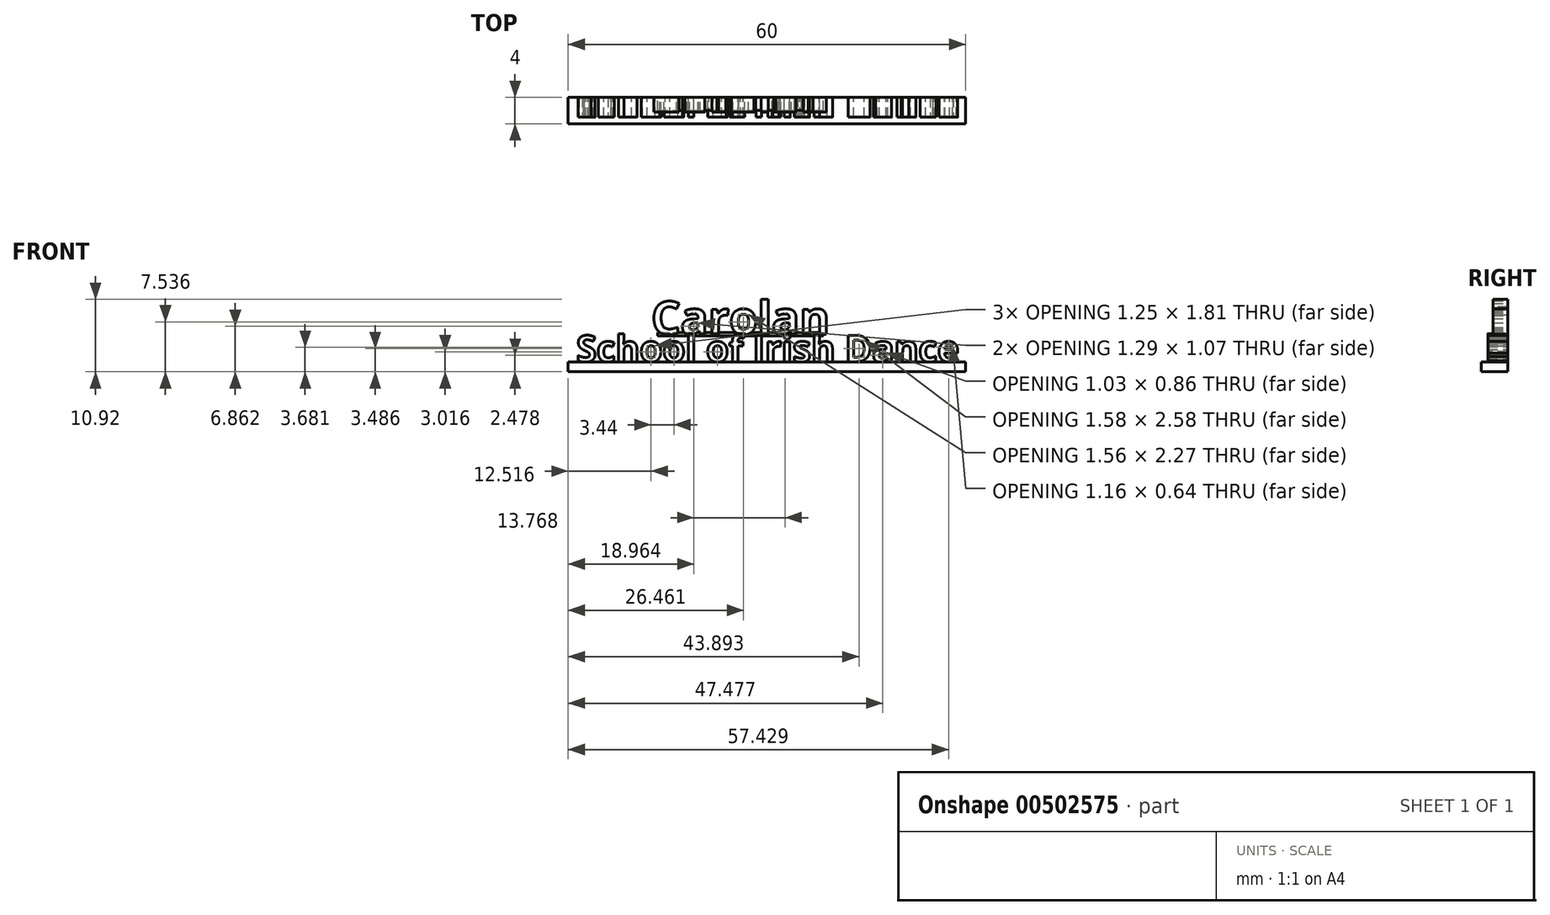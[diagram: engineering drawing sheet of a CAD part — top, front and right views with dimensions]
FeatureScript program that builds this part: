
annotation { "Feature Type Name" : "Feature", "Feature Type Description" : "" }
export const myFeature = defineFeature(function(context is Context, id is Id, definition is map)
    precondition{}
    {
        {
            var Q0;
            Q0=qCreatedBy(makeId("Front.planeOp"),FACE);
            var sketch = newSketch(context, id + "F0", { "sketchPlane" : qUnion([Q0])});
            skLineSegment(sketch, "E0.bottom", {"start": v(-37.8, -3.94) * mm, "end": v(22.2, -3.94) * mm});
            skLineSegment(sketch, "E0.top", {"start": v(-37.8, -5.44) * mm, "end": v(22.2, -5.44) * mm});
            skLineSegment(sketch, "E0.left", {"start": v(-37.8, -3.94) * mm, "end": v(-37.8, -5.44) * mm});
            skLineSegment(sketch, "E0.right", {"start": v(22.2, -3.94) * mm, "end": v(22.2, -5.44) * mm});
            skSolve(sketch);
        }
        {
            var Q0;
            Q0=makeQuery(id+"F0.imprint","IMPRINT",FACE,{"disambiguationData":[TD([[makeQuery(id+"F0.imprint","IMPRINT",EDGE,{"derivedFrom":sQuery(id+"F0.wireOp",EDGE,"E0.bottom")}),-1.0]])]});
            extrude(context, id + "F1", {"entities" : qUnion([Q0]), "depth" : 4 * mm, "offsetDistance" : 25 * mm});
        }
        {
            var Q0;
            Q0=qCreatedBy(makeId("Front.planeOp"),FACE);
            var sketch = newSketch(context, id + "F2", { "sketchPlane" : qUnion([Q0])});
            skText(sketch, "E1", { "text": "School of Irish Dance", "fontName": "OpenSans-Bold.ttf"});
            const initialGuessF2  = {"E1": [-0.02696, 0.00286, 1, 0, 0.004]};
            skSetInitialGuess(sketch, initialGuessF2);
            skSolve(sketch);
        }
        {
            var Q0;
            Q0 = qSketchRegion(id + "F2", true);
            extrude(context, id + "F3", {"entities" : qUnion([Q0]), "depth" : 3 * mm, "offsetDistance" : 25 * mm});
        }
        {
            var Q0;
            Q0=makeQuery(id+"F3.opExtrude","SWEPT_BODY",BODY,{"disambiguationData":[OSD([sQuery(id+"F2.wireOp",EDGE,"E1.sketch_text.stroke-0"),sQuery(id+"F2.wireOp",EDGE,"E1.sketch_text.stroke-1"),sQuery(id+"F2.wireOp",EDGE,"E1.sketch_text.stroke-2"),sQuery(id+"F2.wireOp",EDGE,"E1.sketch_text.stroke-3"),sQuery(id+"F2.wireOp",EDGE,"E1.sketch_text.stroke-4"),sQuery(id+"F2.wireOp",EDGE,"E1.sketch_text.stroke-5"),sQuery(id+"F2.wireOp",EDGE,"E1.sketch_text.stroke-6"),sQuery(id+"F2.wireOp",EDGE,"E1.sketch_text.stroke-7"),sQuery(id+"F2.wireOp",EDGE,"E1.sketch_text.stroke-8"),sQuery(id+"F2.wireOp",EDGE,"E1.sketch_text.stroke-9"),sQuery(id+"F2.wireOp",EDGE,"E1.sketch_text.stroke-10"),sQuery(id+"F2.wireOp",EDGE,"E1.sketch_text.stroke-11"),sQuery(id+"F2.wireOp",EDGE,"E1.sketch_text.stroke-12"),sQuery(id+"F2.wireOp",EDGE,"E1.sketch_text.stroke-13"),sQuery(id+"F2.wireOp",EDGE,"E1.sketch_text.stroke-14"),sQuery(id+"F2.wireOp",EDGE,"E1.sketch_text.stroke-15"),sQuery(id+"F2.wireOp",EDGE,"E1.sketch_text.stroke-16"),sQuery(id+"F2.wireOp",EDGE,"E1.sketch_text.stroke-17"),sQuery(id+"F2.wireOp",EDGE,"E1.sketch_text.stroke-18"),sQuery(id+"F2.wireOp",EDGE,"E1.sketch_text.stroke-19"),sQuery(id+"F2.wireOp",EDGE,"E1.sketch_text.stroke-20"),sQuery(id+"F2.wireOp",EDGE,"E1.sketch_text.stroke-21"),sQuery(id+"F2.wireOp",EDGE,"E1.sketch_text.stroke-22"),sQuery(id+"F2.wireOp",EDGE,"E1.sketch_text.stroke-23"),sQuery(id+"F2.wireOp",EDGE,"E1.sketch_text.stroke-24"),sQuery(id+"F2.wireOp",EDGE,"E1.sketch_text.stroke-25"),sQuery(id+"F2.wireOp",EDGE,"E1.sketch_text.stroke-26"),sQuery(id+"F2.wireOp",EDGE,"E1.sketch_text.stroke-27")])]});
            var Q1;
            Q1=makeQuery(id+"F3.opExtrude","SWEPT_BODY",BODY,{"disambiguationData":[OSD([sQuery(id+"F2.wireOp",EDGE,"E1.sketch_text.stroke-28"),sQuery(id+"F2.wireOp",EDGE,"E1.sketch_text.stroke-29"),sQuery(id+"F2.wireOp",EDGE,"E1.sketch_text.stroke-30"),sQuery(id+"F2.wireOp",EDGE,"E1.sketch_text.stroke-31"),sQuery(id+"F2.wireOp",EDGE,"E1.sketch_text.stroke-32"),sQuery(id+"F2.wireOp",EDGE,"E1.sketch_text.stroke-33"),sQuery(id+"F2.wireOp",EDGE,"E1.sketch_text.stroke-34"),sQuery(id+"F2.wireOp",EDGE,"E1.sketch_text.stroke-35"),sQuery(id+"F2.wireOp",EDGE,"E1.sketch_text.stroke-36"),sQuery(id+"F2.wireOp",EDGE,"E1.sketch_text.stroke-37"),sQuery(id+"F2.wireOp",EDGE,"E1.sketch_text.stroke-38"),sQuery(id+"F2.wireOp",EDGE,"E1.sketch_text.stroke-39"),sQuery(id+"F2.wireOp",EDGE,"E1.sketch_text.stroke-40"),sQuery(id+"F2.wireOp",EDGE,"E1.sketch_text.stroke-41")])]});
            var Q2;
            Q2=makeQuery(id+"F3.opExtrude","SWEPT_BODY",BODY,{"disambiguationData":[OSD([sQuery(id+"F2.wireOp",EDGE,"E1.sketch_text.stroke-42"),sQuery(id+"F2.wireOp",EDGE,"E1.sketch_text.stroke-43"),sQuery(id+"F2.wireOp",EDGE,"E1.sketch_text.stroke-44"),sQuery(id+"F2.wireOp",EDGE,"E1.sketch_text.stroke-45"),sQuery(id+"F2.wireOp",EDGE,"E1.sketch_text.stroke-46"),sQuery(id+"F2.wireOp",EDGE,"E1.sketch_text.stroke-47"),sQuery(id+"F2.wireOp",EDGE,"E1.sketch_text.stroke-48"),sQuery(id+"F2.wireOp",EDGE,"E1.sketch_text.stroke-49"),sQuery(id+"F2.wireOp",EDGE,"E1.sketch_text.stroke-50"),sQuery(id+"F2.wireOp",EDGE,"E1.sketch_text.stroke-51"),sQuery(id+"F2.wireOp",EDGE,"E1.sketch_text.stroke-52"),sQuery(id+"F2.wireOp",EDGE,"E1.sketch_text.stroke-53"),sQuery(id+"F2.wireOp",EDGE,"E1.sketch_text.stroke-54"),sQuery(id+"F2.wireOp",EDGE,"E1.sketch_text.stroke-55"),sQuery(id+"F2.wireOp",EDGE,"E1.sketch_text.stroke-56"),sQuery(id+"F2.wireOp",EDGE,"E1.sketch_text.stroke-57"),sQuery(id+"F2.wireOp",EDGE,"E1.sketch_text.stroke-58")])]});
            var Q3;
            Q3=makeQuery(id+"F3.opExtrude","SWEPT_BODY",BODY,{"disambiguationData":[OSD([sQuery(id+"F2.wireOp",EDGE,"E1.sketch_text.stroke-59"),sQuery(id+"F2.wireOp",EDGE,"E1.sketch_text.stroke-60"),sQuery(id+"F2.wireOp",EDGE,"E1.sketch_text.stroke-61"),sQuery(id+"F2.wireOp",EDGE,"E1.sketch_text.stroke-62"),sQuery(id+"F2.wireOp",EDGE,"E1.sketch_text.stroke-63"),sQuery(id+"F2.wireOp",EDGE,"E1.sketch_text.stroke-64"),sQuery(id+"F2.wireOp",EDGE,"E1.sketch_text.stroke-65"),sQuery(id+"F2.wireOp",EDGE,"E1.sketch_text.stroke-66"),sQuery(id+"F2.wireOp",EDGE,"E1.sketch_text.stroke-67"),sQuery(id+"F2.wireOp",EDGE,"E1.sketch_text.stroke-68"),sQuery(id+"F2.wireOp",EDGE,"E1.sketch_text.stroke-69"),sQuery(id+"F2.wireOp",EDGE,"E1.sketch_text.stroke-70"),sQuery(id+"F2.wireOp",EDGE,"E1.sketch_text.stroke-71"),sQuery(id+"F2.wireOp",EDGE,"E1.sketch_text.stroke-72"),sQuery(id+"F2.wireOp",EDGE,"E1.sketch_text.stroke-73"),sQuery(id+"F2.wireOp",EDGE,"E1.sketch_text.stroke-74"),sQuery(id+"F2.wireOp",EDGE,"E1.sketch_text.stroke-75"),sQuery(id+"F2.wireOp",EDGE,"E1.sketch_text.stroke-76")])]});
            var Q4;
            Q4=makeQuery(id+"F3.opExtrude","SWEPT_BODY",BODY,{"disambiguationData":[OSD([sQuery(id+"F2.wireOp",EDGE,"E1.sketch_text.stroke-77"),sQuery(id+"F2.wireOp",EDGE,"E1.sketch_text.stroke-78"),sQuery(id+"F2.wireOp",EDGE,"E1.sketch_text.stroke-79"),sQuery(id+"F2.wireOp",EDGE,"E1.sketch_text.stroke-80"),sQuery(id+"F2.wireOp",EDGE,"E1.sketch_text.stroke-81"),sQuery(id+"F2.wireOp",EDGE,"E1.sketch_text.stroke-82"),sQuery(id+"F2.wireOp",EDGE,"E1.sketch_text.stroke-83"),sQuery(id+"F2.wireOp",EDGE,"E1.sketch_text.stroke-84"),sQuery(id+"F2.wireOp",EDGE,"E1.sketch_text.stroke-85"),sQuery(id+"F2.wireOp",EDGE,"E1.sketch_text.stroke-86"),sQuery(id+"F2.wireOp",EDGE,"E1.sketch_text.stroke-87"),sQuery(id+"F2.wireOp",EDGE,"E1.sketch_text.stroke-88"),sQuery(id+"F2.wireOp",EDGE,"E1.sketch_text.stroke-89"),sQuery(id+"F2.wireOp",EDGE,"E1.sketch_text.stroke-90"),sQuery(id+"F2.wireOp",EDGE,"E1.sketch_text.stroke-91"),sQuery(id+"F2.wireOp",EDGE,"E1.sketch_text.stroke-92"),sQuery(id+"F2.wireOp",EDGE,"E1.sketch_text.stroke-93"),sQuery(id+"F2.wireOp",EDGE,"E1.sketch_text.stroke-94")])]});
            var Q5;
            Q5=makeQuery(id+"F3.opExtrude","SWEPT_BODY",BODY,{"disambiguationData":[OSD([sQuery(id+"F2.wireOp",EDGE,"E1.sketch_text.stroke-95"),sQuery(id+"F2.wireOp",EDGE,"E1.sketch_text.stroke-96"),sQuery(id+"F2.wireOp",EDGE,"E1.sketch_text.stroke-97"),sQuery(id+"F2.wireOp",EDGE,"E1.sketch_text.stroke-98")])]});
            var Q6;
            Q6=makeQuery(id+"F3.opExtrude","SWEPT_BODY",BODY,{"disambiguationData":[OSD([sQuery(id+"F2.wireOp",EDGE,"E1.sketch_text.stroke-99"),sQuery(id+"F2.wireOp",EDGE,"E1.sketch_text.stroke-100"),sQuery(id+"F2.wireOp",EDGE,"E1.sketch_text.stroke-101"),sQuery(id+"F2.wireOp",EDGE,"E1.sketch_text.stroke-102"),sQuery(id+"F2.wireOp",EDGE,"E1.sketch_text.stroke-103"),sQuery(id+"F2.wireOp",EDGE,"E1.sketch_text.stroke-104"),sQuery(id+"F2.wireOp",EDGE,"E1.sketch_text.stroke-105"),sQuery(id+"F2.wireOp",EDGE,"E1.sketch_text.stroke-106"),sQuery(id+"F2.wireOp",EDGE,"E1.sketch_text.stroke-107"),sQuery(id+"F2.wireOp",EDGE,"E1.sketch_text.stroke-108"),sQuery(id+"F2.wireOp",EDGE,"E1.sketch_text.stroke-109"),sQuery(id+"F2.wireOp",EDGE,"E1.sketch_text.stroke-110"),sQuery(id+"F2.wireOp",EDGE,"E1.sketch_text.stroke-111"),sQuery(id+"F2.wireOp",EDGE,"E1.sketch_text.stroke-112"),sQuery(id+"F2.wireOp",EDGE,"E1.sketch_text.stroke-113"),sQuery(id+"F2.wireOp",EDGE,"E1.sketch_text.stroke-114"),sQuery(id+"F2.wireOp",EDGE,"E1.sketch_text.stroke-115"),sQuery(id+"F2.wireOp",EDGE,"E1.sketch_text.stroke-116")])]});
            var Q7;
            Q7=makeQuery(id+"F3.opExtrude","SWEPT_BODY",BODY,{"disambiguationData":[OSD([sQuery(id+"F2.wireOp",EDGE,"E1.sketch_text.stroke-117"),sQuery(id+"F2.wireOp",EDGE,"E1.sketch_text.stroke-118"),sQuery(id+"F2.wireOp",EDGE,"E1.sketch_text.stroke-119"),sQuery(id+"F2.wireOp",EDGE,"E1.sketch_text.stroke-120"),sQuery(id+"F2.wireOp",EDGE,"E1.sketch_text.stroke-121"),sQuery(id+"F2.wireOp",EDGE,"E1.sketch_text.stroke-122"),sQuery(id+"F2.wireOp",EDGE,"E1.sketch_text.stroke-123"),sQuery(id+"F2.wireOp",EDGE,"E1.sketch_text.stroke-124"),sQuery(id+"F2.wireOp",EDGE,"E1.sketch_text.stroke-125"),sQuery(id+"F2.wireOp",EDGE,"E1.sketch_text.stroke-126"),sQuery(id+"F2.wireOp",EDGE,"E1.sketch_text.stroke-127"),sQuery(id+"F2.wireOp",EDGE,"E1.sketch_text.stroke-128"),sQuery(id+"F2.wireOp",EDGE,"E1.sketch_text.stroke-129"),sQuery(id+"F2.wireOp",EDGE,"E1.sketch_text.stroke-130"),sQuery(id+"F2.wireOp",EDGE,"E1.sketch_text.stroke-131"),sQuery(id+"F2.wireOp",EDGE,"E1.sketch_text.stroke-132"),sQuery(id+"F2.wireOp",EDGE,"E1.sketch_text.stroke-133"),sQuery(id+"F2.wireOp",EDGE,"E1.sketch_text.stroke-134")])]});
            var Q8;
            Q8=makeQuery(id+"F3.opExtrude","SWEPT_BODY",BODY,{"disambiguationData":[OSD([sQuery(id+"F2.wireOp",EDGE,"E1.sketch_text.stroke-135"),sQuery(id+"F2.wireOp",EDGE,"E1.sketch_text.stroke-136"),sQuery(id+"F2.wireOp",EDGE,"E1.sketch_text.stroke-137"),sQuery(id+"F2.wireOp",EDGE,"E1.sketch_text.stroke-138")])]});
            var Q9;
            Q9=makeQuery(id+"F3.opExtrude","SWEPT_BODY",BODY,{"disambiguationData":[OSD([sQuery(id+"F2.wireOp",EDGE,"E1.sketch_text.stroke-139"),sQuery(id+"F2.wireOp",EDGE,"E1.sketch_text.stroke-140"),sQuery(id+"F2.wireOp",EDGE,"E1.sketch_text.stroke-141"),sQuery(id+"F2.wireOp",EDGE,"E1.sketch_text.stroke-142"),sQuery(id+"F2.wireOp",EDGE,"E1.sketch_text.stroke-143"),sQuery(id+"F2.wireOp",EDGE,"E1.sketch_text.stroke-144"),sQuery(id+"F2.wireOp",EDGE,"E1.sketch_text.stroke-145"),sQuery(id+"F2.wireOp",EDGE,"E1.sketch_text.stroke-146"),sQuery(id+"F2.wireOp",EDGE,"E1.sketch_text.stroke-147"),sQuery(id+"F2.wireOp",EDGE,"E1.sketch_text.stroke-148"),sQuery(id+"F2.wireOp",EDGE,"E1.sketch_text.stroke-149"),sQuery(id+"F2.wireOp",EDGE,"E1.sketch_text.stroke-150"),sQuery(id+"F2.wireOp",EDGE,"E1.sketch_text.stroke-151")])]});
            var Q10;
            Q10=makeQuery(id+"F3.opExtrude","SWEPT_BODY",BODY,{"disambiguationData":[OSD([sQuery(id+"F2.wireOp",EDGE,"E1.sketch_text.stroke-152"),sQuery(id+"F2.wireOp",EDGE,"E1.sketch_text.stroke-153"),sQuery(id+"F2.wireOp",EDGE,"E1.sketch_text.stroke-154"),sQuery(id+"F2.wireOp",EDGE,"E1.sketch_text.stroke-155"),sQuery(id+"F2.wireOp",EDGE,"E1.sketch_text.stroke-156")])]});
            var Q11;
            Q11=makeQuery(id+"F3.opExtrude","SWEPT_BODY",BODY,{"disambiguationData":[OSD([sQuery(id+"F2.wireOp",EDGE,"E1.sketch_text.stroke-157"),sQuery(id+"F2.wireOp",EDGE,"E1.sketch_text.stroke-158"),sQuery(id+"F2.wireOp",EDGE,"E1.sketch_text.stroke-159"),sQuery(id+"F2.wireOp",EDGE,"E1.sketch_text.stroke-160")])]});
            var Q12;
            Q12=makeQuery(id+"F3.opExtrude","SWEPT_BODY",BODY,{"disambiguationData":[OSD([sQuery(id+"F2.wireOp",EDGE,"E1.sketch_text.stroke-161"),sQuery(id+"F2.wireOp",EDGE,"E1.sketch_text.stroke-162"),sQuery(id+"F2.wireOp",EDGE,"E1.sketch_text.stroke-163"),sQuery(id+"F2.wireOp",EDGE,"E1.sketch_text.stroke-164"),sQuery(id+"F2.wireOp",EDGE,"E1.sketch_text.stroke-165"),sQuery(id+"F2.wireOp",EDGE,"E1.sketch_text.stroke-166"),sQuery(id+"F2.wireOp",EDGE,"E1.sketch_text.stroke-167"),sQuery(id+"F2.wireOp",EDGE,"E1.sketch_text.stroke-168"),sQuery(id+"F2.wireOp",EDGE,"E1.sketch_text.stroke-169"),sQuery(id+"F2.wireOp",EDGE,"E1.sketch_text.stroke-170"),sQuery(id+"F2.wireOp",EDGE,"E1.sketch_text.stroke-171"),sQuery(id+"F2.wireOp",EDGE,"E1.sketch_text.stroke-172"),sQuery(id+"F2.wireOp",EDGE,"E1.sketch_text.stroke-173"),sQuery(id+"F2.wireOp",EDGE,"E1.sketch_text.stroke-174"),sQuery(id+"F2.wireOp",EDGE,"E1.sketch_text.stroke-175"),sQuery(id+"F2.wireOp",EDGE,"E1.sketch_text.stroke-176"),sQuery(id+"F2.wireOp",EDGE,"E1.sketch_text.stroke-177"),sQuery(id+"F2.wireOp",EDGE,"E1.sketch_text.stroke-178"),sQuery(id+"F2.wireOp",EDGE,"E1.sketch_text.stroke-179"),sQuery(id+"F2.wireOp",EDGE,"E1.sketch_text.stroke-180"),sQuery(id+"F2.wireOp",EDGE,"E1.sketch_text.stroke-181"),sQuery(id+"F2.wireOp",EDGE,"E1.sketch_text.stroke-182"),sQuery(id+"F2.wireOp",EDGE,"E1.sketch_text.stroke-183"),sQuery(id+"F2.wireOp",EDGE,"E1.sketch_text.stroke-184"),sQuery(id+"F2.wireOp",EDGE,"E1.sketch_text.stroke-185"),sQuery(id+"F2.wireOp",EDGE,"E1.sketch_text.stroke-186")])]});
            var Q13;
            Q13=makeQuery(id+"F3.opExtrude","SWEPT_BODY",BODY,{"disambiguationData":[OSD([sQuery(id+"F2.wireOp",EDGE,"E1.sketch_text.stroke-187"),sQuery(id+"F2.wireOp",EDGE,"E1.sketch_text.stroke-188"),sQuery(id+"F2.wireOp",EDGE,"E1.sketch_text.stroke-189"),sQuery(id+"F2.wireOp",EDGE,"E1.sketch_text.stroke-190"),sQuery(id+"F2.wireOp",EDGE,"E1.sketch_text.stroke-191"),sQuery(id+"F2.wireOp",EDGE,"E1.sketch_text.stroke-192"),sQuery(id+"F2.wireOp",EDGE,"E1.sketch_text.stroke-193"),sQuery(id+"F2.wireOp",EDGE,"E1.sketch_text.stroke-194"),sQuery(id+"F2.wireOp",EDGE,"E1.sketch_text.stroke-195"),sQuery(id+"F2.wireOp",EDGE,"E1.sketch_text.stroke-196"),sQuery(id+"F2.wireOp",EDGE,"E1.sketch_text.stroke-197"),sQuery(id+"F2.wireOp",EDGE,"E1.sketch_text.stroke-198"),sQuery(id+"F2.wireOp",EDGE,"E1.sketch_text.stroke-199"),sQuery(id+"F2.wireOp",EDGE,"E1.sketch_text.stroke-200"),sQuery(id+"F2.wireOp",EDGE,"E1.sketch_text.stroke-201"),sQuery(id+"F2.wireOp",EDGE,"E1.sketch_text.stroke-202"),sQuery(id+"F2.wireOp",EDGE,"E1.sketch_text.stroke-203")])]});
            var Q14;
            Q14=makeQuery(id+"F3.opExtrude","SWEPT_BODY",BODY,{"disambiguationData":[OSD([sQuery(id+"F2.wireOp",EDGE,"E1.sketch_text.stroke-204"),sQuery(id+"F2.wireOp",EDGE,"E1.sketch_text.stroke-205"),sQuery(id+"F2.wireOp",EDGE,"E1.sketch_text.stroke-206"),sQuery(id+"F2.wireOp",EDGE,"E1.sketch_text.stroke-207"),sQuery(id+"F2.wireOp",EDGE,"E1.sketch_text.stroke-208"),sQuery(id+"F2.wireOp",EDGE,"E1.sketch_text.stroke-209"),sQuery(id+"F2.wireOp",EDGE,"E1.sketch_text.stroke-210"),sQuery(id+"F2.wireOp",EDGE,"E1.sketch_text.stroke-211"),sQuery(id+"F2.wireOp",EDGE,"E1.sketch_text.stroke-212"),sQuery(id+"F2.wireOp",EDGE,"E1.sketch_text.stroke-213"),sQuery(id+"F2.wireOp",EDGE,"E1.sketch_text.stroke-214"),sQuery(id+"F2.wireOp",EDGE,"E1.sketch_text.stroke-215")])]});
            var Q15;
            Q15=makeQuery(id+"F3.opExtrude","SWEPT_BODY",BODY,{"disambiguationData":[OSD([sQuery(id+"F2.wireOp",EDGE,"E1.sketch_text.stroke-216"),sQuery(id+"F2.wireOp",EDGE,"E1.sketch_text.stroke-217"),sQuery(id+"F2.wireOp",EDGE,"E1.sketch_text.stroke-218"),sQuery(id+"F2.wireOp",EDGE,"E1.sketch_text.stroke-219"),sQuery(id+"F2.wireOp",EDGE,"E1.sketch_text.stroke-220"),sQuery(id+"F2.wireOp",EDGE,"E1.sketch_text.stroke-221"),sQuery(id+"F2.wireOp",EDGE,"E1.sketch_text.stroke-222"),sQuery(id+"F2.wireOp",EDGE,"E1.sketch_text.stroke-223"),sQuery(id+"F2.wireOp",EDGE,"E1.sketch_text.stroke-224"),sQuery(id+"F2.wireOp",EDGE,"E1.sketch_text.stroke-225"),sQuery(id+"F2.wireOp",EDGE,"E1.sketch_text.stroke-226"),sQuery(id+"F2.wireOp",EDGE,"E1.sketch_text.stroke-227"),sQuery(id+"F2.wireOp",EDGE,"E1.sketch_text.stroke-228"),sQuery(id+"F2.wireOp",EDGE,"E1.sketch_text.stroke-229"),sQuery(id+"F2.wireOp",EDGE,"E1.sketch_text.stroke-230"),sQuery(id+"F2.wireOp",EDGE,"E1.sketch_text.stroke-231"),sQuery(id+"F2.wireOp",EDGE,"E1.sketch_text.stroke-232"),sQuery(id+"F2.wireOp",EDGE,"E1.sketch_text.stroke-233"),sQuery(id+"F2.wireOp",EDGE,"E1.sketch_text.stroke-234"),sQuery(id+"F2.wireOp",EDGE,"E1.sketch_text.stroke-235"),sQuery(id+"F2.wireOp",EDGE,"E1.sketch_text.stroke-236"),sQuery(id+"F2.wireOp",EDGE,"E1.sketch_text.stroke-237"),sQuery(id+"F2.wireOp",EDGE,"E1.sketch_text.stroke-238"),sQuery(id+"F2.wireOp",EDGE,"E1.sketch_text.stroke-239"),sQuery(id+"F2.wireOp",EDGE,"E1.sketch_text.stroke-240")])]});
            var Q16;
            Q16=makeQuery(id+"F3.opExtrude","SWEPT_BODY",BODY,{"disambiguationData":[OSD([sQuery(id+"F2.wireOp",EDGE,"E1.sketch_text.stroke-241"),sQuery(id+"F2.wireOp",EDGE,"E1.sketch_text.stroke-242"),sQuery(id+"F2.wireOp",EDGE,"E1.sketch_text.stroke-243"),sQuery(id+"F2.wireOp",EDGE,"E1.sketch_text.stroke-244"),sQuery(id+"F2.wireOp",EDGE,"E1.sketch_text.stroke-245"),sQuery(id+"F2.wireOp",EDGE,"E1.sketch_text.stroke-246"),sQuery(id+"F2.wireOp",EDGE,"E1.sketch_text.stroke-247"),sQuery(id+"F2.wireOp",EDGE,"E1.sketch_text.stroke-248"),sQuery(id+"F2.wireOp",EDGE,"E1.sketch_text.stroke-249"),sQuery(id+"F2.wireOp",EDGE,"E1.sketch_text.stroke-250"),sQuery(id+"F2.wireOp",EDGE,"E1.sketch_text.stroke-251"),sQuery(id+"F2.wireOp",EDGE,"E1.sketch_text.stroke-252"),sQuery(id+"F2.wireOp",EDGE,"E1.sketch_text.stroke-253"),sQuery(id+"F2.wireOp",EDGE,"E1.sketch_text.stroke-254"),sQuery(id+"F2.wireOp",EDGE,"E1.sketch_text.stroke-255"),sQuery(id+"F2.wireOp",EDGE,"E1.sketch_text.stroke-256"),sQuery(id+"F2.wireOp",EDGE,"E1.sketch_text.stroke-257")])]});
            var Q17;
            Q17=makeQuery(id+"F3.opExtrude","SWEPT_BODY",BODY,{"disambiguationData":[OSD([sQuery(id+"F2.wireOp",EDGE,"E1.sketch_text.stroke-258"),sQuery(id+"F2.wireOp",EDGE,"E1.sketch_text.stroke-259"),sQuery(id+"F2.wireOp",EDGE,"E1.sketch_text.stroke-260"),sQuery(id+"F2.wireOp",EDGE,"E1.sketch_text.stroke-261"),sQuery(id+"F2.wireOp",EDGE,"E1.sketch_text.stroke-262"),sQuery(id+"F2.wireOp",EDGE,"E1.sketch_text.stroke-263"),sQuery(id+"F2.wireOp",EDGE,"E1.sketch_text.stroke-264"),sQuery(id+"F2.wireOp",EDGE,"E1.sketch_text.stroke-265"),sQuery(id+"F2.wireOp",EDGE,"E1.sketch_text.stroke-266"),sQuery(id+"F2.wireOp",EDGE,"E1.sketch_text.stroke-267"),sQuery(id+"F2.wireOp",EDGE,"E1.sketch_text.stroke-268"),sQuery(id+"F2.wireOp",EDGE,"E1.sketch_text.stroke-269"),sQuery(id+"F2.wireOp",EDGE,"E1.sketch_text.stroke-270"),sQuery(id+"F2.wireOp",EDGE,"E1.sketch_text.stroke-271")])]});
            var Q18;
            Q18=makeQuery(id+"F3.opExtrude","SWEPT_BODY",BODY,{"disambiguationData":[OSD([sQuery(id+"F2.wireOp",EDGE,"E1.sketch_text.stroke-272"),sQuery(id+"F2.wireOp",EDGE,"E1.sketch_text.stroke-273"),sQuery(id+"F2.wireOp",EDGE,"E1.sketch_text.stroke-274"),sQuery(id+"F2.wireOp",EDGE,"E1.sketch_text.stroke-275"),sQuery(id+"F2.wireOp",EDGE,"E1.sketch_text.stroke-276"),sQuery(id+"F2.wireOp",EDGE,"E1.sketch_text.stroke-277"),sQuery(id+"F2.wireOp",EDGE,"E1.sketch_text.stroke-278"),sQuery(id+"F2.wireOp",EDGE,"E1.sketch_text.stroke-279"),sQuery(id+"F2.wireOp",EDGE,"E1.sketch_text.stroke-280"),sQuery(id+"F2.wireOp",EDGE,"E1.sketch_text.stroke-281"),sQuery(id+"F2.wireOp",EDGE,"E1.sketch_text.stroke-282"),sQuery(id+"F2.wireOp",EDGE,"E1.sketch_text.stroke-283"),sQuery(id+"F2.wireOp",EDGE,"E1.sketch_text.stroke-284"),sQuery(id+"F2.wireOp",EDGE,"E1.sketch_text.stroke-285"),sQuery(id+"F2.wireOp",EDGE,"E1.sketch_text.stroke-286"),sQuery(id+"F2.wireOp",EDGE,"E1.sketch_text.stroke-287"),sQuery(id+"F2.wireOp",EDGE,"E1.sketch_text.stroke-288"),sQuery(id+"F2.wireOp",EDGE,"E1.sketch_text.stroke-289"),sQuery(id+"F2.wireOp",EDGE,"E1.sketch_text.stroke-290"),sQuery(id+"F2.wireOp",EDGE,"E1.sketch_text.stroke-291")])]});
            transform(context, id + "F4", {"entities" : qUnion([Q0, Q1, Q2, Q3, Q4, Q5, Q6, Q7, Q8, Q9, Q10, Q11, Q12, Q13, Q14, Q15, Q16, Q17, Q18]), "transformType" : TransformType.TRANSLATION_3D, "dx" : 8 * mm, "dy" : 0 * mm, "dz" : -6.8 * mm, "makeCopy" : false});
        }
        {
            var Q0;
            Q0=qCreatedBy(makeId("Front.planeOp"),FACE);
            var sketch = newSketch(context, id + "F5", { "sketchPlane" : qUnion([Q0])});
            skText(sketch, "E2", { "text": "Carolan", "fontName": "OpenSans-Bold.ttf"});
            const initialGuessF5  = {"E2": [-0.00875, 0.005, 1, 0, 0.005]};
            skSetInitialGuess(sketch, initialGuessF5);
            skSolve(sketch);
        }
        {
            var Q0;
            Q0 = qSketchRegion(id + "F5", true);
            extrude(context, id + "F6", {"entities" : qUnion([Q0]), "depth" : 2.2 * mm, "offsetDistance" : 25 * mm});
        }
        {
            var Q0;
            Q0=makeQuery(id+"F6.opExtrude","SWEPT_BODY",BODY,{"disambiguationData":[OSD([sQuery(id+"F5.wireOp",EDGE,"E2.sketch_text.stroke-100"),sQuery(id+"F5.wireOp",EDGE,"E2.sketch_text.stroke-101"),sQuery(id+"F5.wireOp",EDGE,"E2.sketch_text.stroke-102"),sQuery(id+"F5.wireOp",EDGE,"E2.sketch_text.stroke-103"),sQuery(id+"F5.wireOp",EDGE,"E2.sketch_text.stroke-104"),sQuery(id+"F5.wireOp",EDGE,"E2.sketch_text.stroke-105"),sQuery(id+"F5.wireOp",EDGE,"E2.sketch_text.stroke-106"),sQuery(id+"F5.wireOp",EDGE,"E2.sketch_text.stroke-107"),sQuery(id+"F5.wireOp",EDGE,"E2.sketch_text.stroke-108"),sQuery(id+"F5.wireOp",EDGE,"E2.sketch_text.stroke-109"),sQuery(id+"F5.wireOp",EDGE,"E2.sketch_text.stroke-110"),sQuery(id+"F5.wireOp",EDGE,"E2.sketch_text.stroke-111"),sQuery(id+"F5.wireOp",EDGE,"E2.sketch_text.stroke-112"),sQuery(id+"F5.wireOp",EDGE,"E2.sketch_text.stroke-113"),sQuery(id+"F5.wireOp",EDGE,"E2.sketch_text.stroke-114"),sQuery(id+"F5.wireOp",EDGE,"E2.sketch_text.stroke-115"),sQuery(id+"F5.wireOp",EDGE,"E2.sketch_text.stroke-116")])]});
            var Q1;
            Q1=makeQuery(id+"F6.opExtrude","SWEPT_BODY",BODY,{"disambiguationData":[OSD([sQuery(id+"F5.wireOp",EDGE,"E2.sketch_text.stroke-75"),sQuery(id+"F5.wireOp",EDGE,"E2.sketch_text.stroke-76"),sQuery(id+"F5.wireOp",EDGE,"E2.sketch_text.stroke-77"),sQuery(id+"F5.wireOp",EDGE,"E2.sketch_text.stroke-78"),sQuery(id+"F5.wireOp",EDGE,"E2.sketch_text.stroke-79"),sQuery(id+"F5.wireOp",EDGE,"E2.sketch_text.stroke-80"),sQuery(id+"F5.wireOp",EDGE,"E2.sketch_text.stroke-81"),sQuery(id+"F5.wireOp",EDGE,"E2.sketch_text.stroke-82"),sQuery(id+"F5.wireOp",EDGE,"E2.sketch_text.stroke-83"),sQuery(id+"F5.wireOp",EDGE,"E2.sketch_text.stroke-84"),sQuery(id+"F5.wireOp",EDGE,"E2.sketch_text.stroke-85"),sQuery(id+"F5.wireOp",EDGE,"E2.sketch_text.stroke-86"),sQuery(id+"F5.wireOp",EDGE,"E2.sketch_text.stroke-87"),sQuery(id+"F5.wireOp",EDGE,"E2.sketch_text.stroke-88"),sQuery(id+"F5.wireOp",EDGE,"E2.sketch_text.stroke-89"),sQuery(id+"F5.wireOp",EDGE,"E2.sketch_text.stroke-90"),sQuery(id+"F5.wireOp",EDGE,"E2.sketch_text.stroke-91"),sQuery(id+"F5.wireOp",EDGE,"E2.sketch_text.stroke-92"),sQuery(id+"F5.wireOp",EDGE,"E2.sketch_text.stroke-93"),sQuery(id+"F5.wireOp",EDGE,"E2.sketch_text.stroke-94"),sQuery(id+"F5.wireOp",EDGE,"E2.sketch_text.stroke-95"),sQuery(id+"F5.wireOp",EDGE,"E2.sketch_text.stroke-96"),sQuery(id+"F5.wireOp",EDGE,"E2.sketch_text.stroke-97"),sQuery(id+"F5.wireOp",EDGE,"E2.sketch_text.stroke-98"),sQuery(id+"F5.wireOp",EDGE,"E2.sketch_text.stroke-99")])]});
            var Q2;
            Q2=makeQuery(id+"F6.opExtrude","SWEPT_BODY",BODY,{"disambiguationData":[OSD([sQuery(id+"F5.wireOp",EDGE,"E2.sketch_text.stroke-71"),sQuery(id+"F5.wireOp",EDGE,"E2.sketch_text.stroke-72"),sQuery(id+"F5.wireOp",EDGE,"E2.sketch_text.stroke-73"),sQuery(id+"F5.wireOp",EDGE,"E2.sketch_text.stroke-74")])]});
            var Q3;
            Q3=makeQuery(id+"F6.opExtrude","SWEPT_BODY",BODY,{"disambiguationData":[OSD([sQuery(id+"F5.wireOp",EDGE,"E2.sketch_text.stroke-53"),sQuery(id+"F5.wireOp",EDGE,"E2.sketch_text.stroke-54"),sQuery(id+"F5.wireOp",EDGE,"E2.sketch_text.stroke-55"),sQuery(id+"F5.wireOp",EDGE,"E2.sketch_text.stroke-56"),sQuery(id+"F5.wireOp",EDGE,"E2.sketch_text.stroke-57"),sQuery(id+"F5.wireOp",EDGE,"E2.sketch_text.stroke-58"),sQuery(id+"F5.wireOp",EDGE,"E2.sketch_text.stroke-59"),sQuery(id+"F5.wireOp",EDGE,"E2.sketch_text.stroke-60"),sQuery(id+"F5.wireOp",EDGE,"E2.sketch_text.stroke-61"),sQuery(id+"F5.wireOp",EDGE,"E2.sketch_text.stroke-62"),sQuery(id+"F5.wireOp",EDGE,"E2.sketch_text.stroke-63"),sQuery(id+"F5.wireOp",EDGE,"E2.sketch_text.stroke-64"),sQuery(id+"F5.wireOp",EDGE,"E2.sketch_text.stroke-65"),sQuery(id+"F5.wireOp",EDGE,"E2.sketch_text.stroke-66"),sQuery(id+"F5.wireOp",EDGE,"E2.sketch_text.stroke-67"),sQuery(id+"F5.wireOp",EDGE,"E2.sketch_text.stroke-68"),sQuery(id+"F5.wireOp",EDGE,"E2.sketch_text.stroke-69"),sQuery(id+"F5.wireOp",EDGE,"E2.sketch_text.stroke-70")])]});
            var Q4;
            Q4=makeQuery(id+"F6.opExtrude","SWEPT_BODY",BODY,{"disambiguationData":[OSD([sQuery(id+"F5.wireOp",EDGE,"E2.sketch_text.stroke-40"),sQuery(id+"F5.wireOp",EDGE,"E2.sketch_text.stroke-41"),sQuery(id+"F5.wireOp",EDGE,"E2.sketch_text.stroke-42"),sQuery(id+"F5.wireOp",EDGE,"E2.sketch_text.stroke-43"),sQuery(id+"F5.wireOp",EDGE,"E2.sketch_text.stroke-44"),sQuery(id+"F5.wireOp",EDGE,"E2.sketch_text.stroke-45"),sQuery(id+"F5.wireOp",EDGE,"E2.sketch_text.stroke-46"),sQuery(id+"F5.wireOp",EDGE,"E2.sketch_text.stroke-47"),sQuery(id+"F5.wireOp",EDGE,"E2.sketch_text.stroke-48"),sQuery(id+"F5.wireOp",EDGE,"E2.sketch_text.stroke-49"),sQuery(id+"F5.wireOp",EDGE,"E2.sketch_text.stroke-50"),sQuery(id+"F5.wireOp",EDGE,"E2.sketch_text.stroke-51"),sQuery(id+"F5.wireOp",EDGE,"E2.sketch_text.stroke-52")])]});
            var Q5;
            Q5=makeQuery(id+"F6.opExtrude","SWEPT_BODY",BODY,{"disambiguationData":[OSD([sQuery(id+"F5.wireOp",EDGE,"E2.sketch_text.stroke-15"),sQuery(id+"F5.wireOp",EDGE,"E2.sketch_text.stroke-16"),sQuery(id+"F5.wireOp",EDGE,"E2.sketch_text.stroke-17"),sQuery(id+"F5.wireOp",EDGE,"E2.sketch_text.stroke-18"),sQuery(id+"F5.wireOp",EDGE,"E2.sketch_text.stroke-19"),sQuery(id+"F5.wireOp",EDGE,"E2.sketch_text.stroke-20"),sQuery(id+"F5.wireOp",EDGE,"E2.sketch_text.stroke-21"),sQuery(id+"F5.wireOp",EDGE,"E2.sketch_text.stroke-22"),sQuery(id+"F5.wireOp",EDGE,"E2.sketch_text.stroke-23"),sQuery(id+"F5.wireOp",EDGE,"E2.sketch_text.stroke-24"),sQuery(id+"F5.wireOp",EDGE,"E2.sketch_text.stroke-25"),sQuery(id+"F5.wireOp",EDGE,"E2.sketch_text.stroke-26"),sQuery(id+"F5.wireOp",EDGE,"E2.sketch_text.stroke-27"),sQuery(id+"F5.wireOp",EDGE,"E2.sketch_text.stroke-28"),sQuery(id+"F5.wireOp",EDGE,"E2.sketch_text.stroke-29"),sQuery(id+"F5.wireOp",EDGE,"E2.sketch_text.stroke-30"),sQuery(id+"F5.wireOp",EDGE,"E2.sketch_text.stroke-31"),sQuery(id+"F5.wireOp",EDGE,"E2.sketch_text.stroke-32"),sQuery(id+"F5.wireOp",EDGE,"E2.sketch_text.stroke-33"),sQuery(id+"F5.wireOp",EDGE,"E2.sketch_text.stroke-34"),sQuery(id+"F5.wireOp",EDGE,"E2.sketch_text.stroke-35"),sQuery(id+"F5.wireOp",EDGE,"E2.sketch_text.stroke-36"),sQuery(id+"F5.wireOp",EDGE,"E2.sketch_text.stroke-37"),sQuery(id+"F5.wireOp",EDGE,"E2.sketch_text.stroke-38"),sQuery(id+"F5.wireOp",EDGE,"E2.sketch_text.stroke-39")])]});
            var Q6;
            Q6=makeQuery(id+"F6.opExtrude","SWEPT_BODY",BODY,{"disambiguationData":[OSD([sQuery(id+"F5.wireOp",EDGE,"E2.sketch_text.stroke-0"),sQuery(id+"F5.wireOp",EDGE,"E2.sketch_text.stroke-1"),sQuery(id+"F5.wireOp",EDGE,"E2.sketch_text.stroke-2"),sQuery(id+"F5.wireOp",EDGE,"E2.sketch_text.stroke-3"),sQuery(id+"F5.wireOp",EDGE,"E2.sketch_text.stroke-4"),sQuery(id+"F5.wireOp",EDGE,"E2.sketch_text.stroke-5"),sQuery(id+"F5.wireOp",EDGE,"E2.sketch_text.stroke-6"),sQuery(id+"F5.wireOp",EDGE,"E2.sketch_text.stroke-7"),sQuery(id+"F5.wireOp",EDGE,"E2.sketch_text.stroke-8"),sQuery(id+"F5.wireOp",EDGE,"E2.sketch_text.stroke-9"),sQuery(id+"F5.wireOp",EDGE,"E2.sketch_text.stroke-10"),sQuery(id+"F5.wireOp",EDGE,"E2.sketch_text.stroke-11"),sQuery(id+"F5.wireOp",EDGE,"E2.sketch_text.stroke-12"),sQuery(id+"F5.wireOp",EDGE,"E2.sketch_text.stroke-13"),sQuery(id+"F5.wireOp",EDGE,"E2.sketch_text.stroke-14")])]});
            transform(context, id + "F7", {"entities" : qUnion([Q0, Q1, Q2, Q3, Q4, Q5, Q6]), "transformType" : TransformType.TRANSLATION_3D, "dx" : 1.1 * mm, "dy" : 0 * mm, "dz" : -4.8 * mm, "makeCopy" : false});
        }
        {
            var Q0;
            Q0=qCreatedBy(makeId("Front.planeOp"),FACE);
            var sketch = newSketch(context, id + "F8", { "sketchPlane" : qUnion([Q0])});
            skLineSegment(sketch, "E3.bottom", {"start": v(-11.3, 0.5) * mm, "end": v(13.7, 0.5) * mm});
            skLineSegment(sketch, "E3.top", {"start": v(-11.3, 0) * mm, "end": v(13.7, 0) * mm});
            skLineSegment(sketch, "E3.left", {"start": v(-11.3, 0.5) * mm, "end": v(-11.3, 0) * mm});
            skLineSegment(sketch, "E3.right", {"start": v(13.7, 0.5) * mm, "end": v(13.7, 0) * mm});
            skSolve(sketch);
        }
        {
            var Q0;
            Q0 = qSketchRegion(id + "F8", true);
            extrude(context, id + "F9", {"entities" : qUnion([Q0]), "depth" : 2 * mm, "offsetDistance" : 25 * mm});
        }
        {
            var Q0;
            Q0=makeQuery(id+"F9.opExtrude","SWEPT_BODY",BODY,{"disambiguationData":[OSD([sQuery(id+"F8.wireOp",EDGE,"E3.bottom"),sQuery(id+"F8.wireOp",EDGE,"E3.top"),sQuery(id+"F8.wireOp",EDGE,"E3.left"),sQuery(id+"F8.wireOp",EDGE,"E3.right")])]});
            transform(context, id + "F10", {"entities" : qUnion([Q0]), "transformType" : TransformType.TRANSLATION_3D, "dx" : 4.63 * mm, "dy" : 0 * mm, "dz" : 0 * mm, "makeCopy" : false});
        }
        {
            var Q0;
            Q0=makeQuery(id+"F1.opExtrude","SWEPT_BODY",BODY,{"disambiguationData":[OSD([sQuery(id+"F0.wireOp",EDGE,"E0.bottom"),sQuery(id+"F0.wireOp",EDGE,"E0.top"),sQuery(id+"F0.wireOp",EDGE,"E0.left"),sQuery(id+"F0.wireOp",EDGE,"E0.right")])]});
            transform(context, id + "F11", {"entities" : qUnion([Q0]), "transformType" : TransformType.TRANSLATION_3D, "dx" : 17.6 * mm, "dy" : 0 * mm, "dz" : 0 * mm, "makeCopy" : false});
        }
    });
